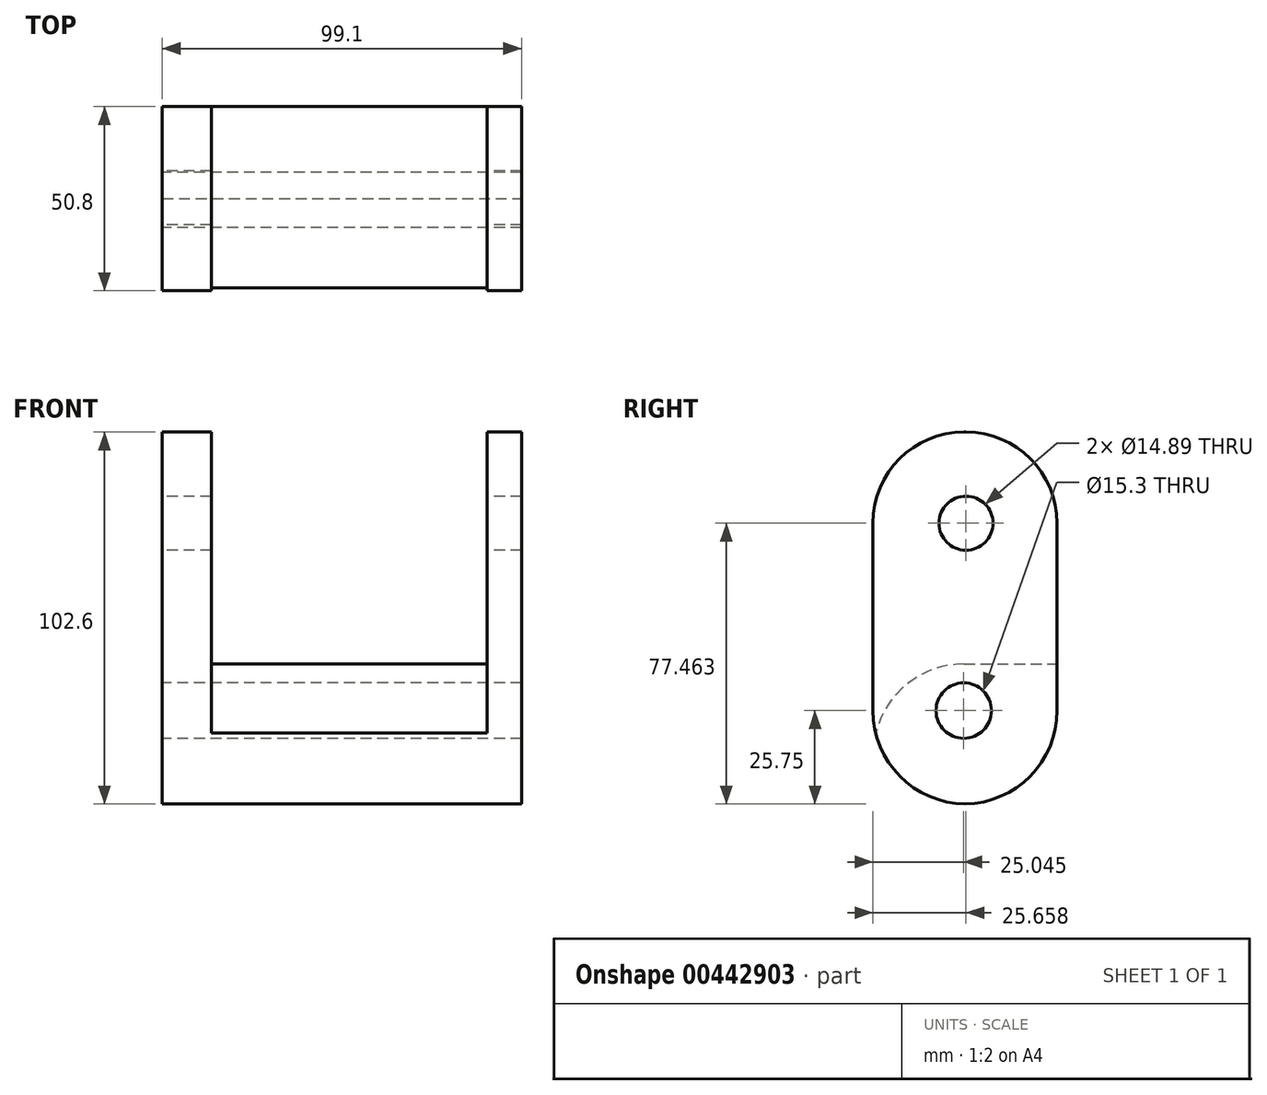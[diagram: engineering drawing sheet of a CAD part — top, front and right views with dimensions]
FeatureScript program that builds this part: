
annotation { "Feature Type Name" : "Feature", "Feature Type Description" : "" }
export const myFeature = defineFeature(function(context is Context, id is Id, definition is map)
    precondition{}
    {
        {
            var Q0;
            Q0=qCreatedBy(makeId("Front.planeOp"),FACE);
            var sketch = newSketch(context, id + "F0", { "sketchPlane" : qUnion([Q0])});
            skLineSegment(sketch, "E0.bottom", {"start": v(-49.55, 51.3) * mm, "end": v(49.55, 51.3) * mm});
            skLineSegment(sketch, "E0.top", {"start": v(-49.55, -51.3) * mm, "end": v(49.55, -51.3) * mm});
            skLineSegment(sketch, "E0.left", {"start": v(-49.55, 51.3) * mm, "end": v(-49.55, -51.3) * mm});
            skLineSegment(sketch, "E0.right", {"start": v(49.55, 51.3) * mm, "end": v(49.55, -51.3) * mm});
            skPoint(sketch, "E0.middle", {"position": v(0, 0) * mm});
            skSolve(sketch);
        }
        {
            var Q0;
            Q0=makeQuery(id+"F0.imprint","IMPRINT",FACE,{"disambiguationData":[TD([[makeQuery(id+"F0.imprint","IMPRINT",EDGE,{"derivedFrom":sQuery(id+"F0.wireOp",EDGE,"E0.bottom")}),-1.0]])]});
            extrude(context, id + "F1", {"entities" : qUnion([Q0]), "depth" : 50.8 * mm});
        }
        {
            var Q0;
            Q0=makeQuery(id+"F1.opExtrude","CAP_EDGE",EDGE,{"disambiguationData":[OSD([sQuery(id+"F0.wireOp",EDGE,"E0.bottom")])],"isStart":false});
            var Q1;
            Q1=makeQuery(id+"F1.opExtrude","CAP_EDGE",EDGE,{"disambiguationData":[OSD([sQuery(id+"F0.wireOp",EDGE,"E0.bottom")])],"isStart":true});
            fillet(context, id + "F2", {"entities" : qUnion([Q0, Q1]), "radius" : 25.14 * mm, "tangentPropagation" : true, "allowEdgeOverflow" : false});
        }
        {
            var Q0;
            Q0=makeQuery(id+"F1.opExtrude","CAP_EDGE",EDGE,{"disambiguationData":[OSD([sQuery(id+"F0.wireOp",EDGE,"E0.top")])],"isStart":true});
            var Q1;
            Q1=makeQuery(id+"F1.opExtrude","CAP_EDGE",EDGE,{"disambiguationData":[OSD([sQuery(id+"F0.wireOp",EDGE,"E0.top")])],"isStart":false});
            fillet(context, id + "F3", {"entities" : qUnion([Q0, Q1]), "radius" : 25.75 * mm, "tangentPropagation" : true, "allowEdgeOverflow" : false});
        }
        {
            var Q0;
            Q0=makeQuery(id+"F1.opExtrude","SWEPT_FACE",FACE,{"disambiguationData":[OSD([sQuery(id+"F0.wireOp",EDGE,"E0.left")])]});
            var sketch = newSketch(context, id + "F4", { "sketchPlane" : qUnion([Q0])});
            skCircle(sketch, "E1", {"center": v(25.14, 26.16) * mm, "radius": 7.45 * mm});
            skCircle(sketch, "E2", {"center": v(25.75, -25.55) * mm, "radius": 7.65 * mm});
            skSolve(sketch);
        }
        {
            var Q0;
            Q0 = qSketchRegion(id + "F4", true);
            extrude(context, id + "F5", {"entities" : qUnion([Q0]), "operationType" : NewBodyOperationType.REMOVE, "oppositeDirection" : true, "depth" : 155.45 * mm});
        }
        {
            var Q0;
            Q0=qCreatedBy(makeId("Front.planeOp"),FACE);
            var sketch = newSketch(context, id + "F6", { "sketchPlane" : qUnion([Q0])});
            skLineSegment(sketch, "E3", {"start": v(40.05, 57.5) * mm, "end": v(40.05, -12.7) * mm});
            skLineSegment(sketch, "E4", {"start": v(40.05, -12.7) * mm, "end": v(-36.07, -12.7) * mm});
            skLineSegment(sketch, "E5", {"start": v(-36.07, -12.7) * mm, "end": v(-36.07, 57.5) * mm});
            skLineSegment(sketch, "E6", {"start": v(-36.07, 57.5) * mm, "end": v(40.05, 57.5) * mm});
            skSolve(sketch);
        }
        {
            var Q0;
            Q0 = qSketchRegion(id + "F6", true);
            extrude(context, id + "F7", {"entities" : qUnion([Q0]), "operationType" : NewBodyOperationType.REMOVE, "depth" : 112.27 * mm});
        }
        {
            var Q0;
            Q0=makeQuery(id+"F7.boolean.opBoolean","INTERSECT",EDGE,{"derivedFrom":[makeQuery(id+"F1.opExtrude","CAP_FACE",FACE,{"disambiguationData":[OSD([sQuery(id+"F0.wireOp",EDGE,"E0.bottom"),sQuery(id+"F0.wireOp",EDGE,"E0.top"),sQuery(id+"F0.wireOp",EDGE,"E0.left"),sQuery(id+"F0.wireOp",EDGE,"E0.right")])],"isStart":false}),makeQuery(id+"F7.opExtrude","SWEPT_FACE",FACE,{"disambiguationData":[OSD([sQuery(id+"F6.wireOp",EDGE,"E4")])]})]});
            var Q1;
            Q1=makeQuery(id+"F7.boolean.opBoolean","COPY",EDGE,{"derivedFrom":makeQuery(id+"F7.opExtrude","CAP_EDGE",EDGE,{"disambiguationData":[OSD([sQuery(id+"F6.wireOp",EDGE,"E4")])],"isStart":true})});
            fillet(context, id + "F8", {"entities" : qUnion([Q0, Q1]), "radius" : 25.14 * mm, "tangentPropagation" : true, "allowEdgeOverflow" : false});
        }
    });
